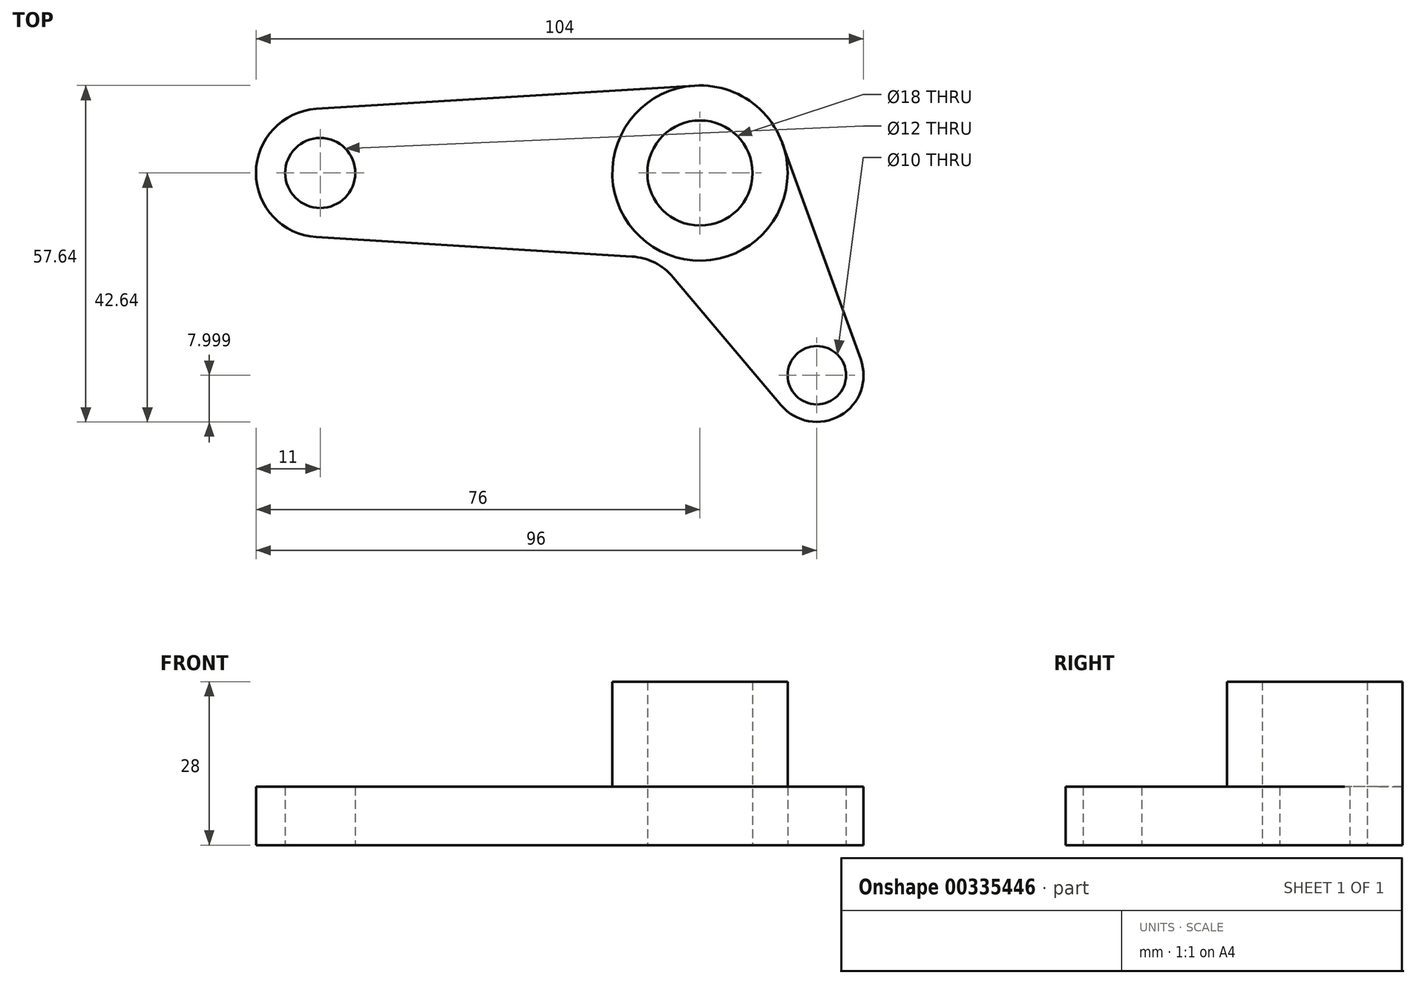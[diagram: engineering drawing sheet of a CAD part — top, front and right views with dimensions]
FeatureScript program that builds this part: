
annotation { "Feature Type Name" : "Feature", "Feature Type Description" : "" }
export const myFeature = defineFeature(function(context is Context, id is Id, definition is map)
    precondition{}
    {
        {
            var Q0;
            Q0=qCreatedBy(makeId("Top.planeOp"),FACE);
            var sketch = newSketch(context, id + "F0", { "sketchPlane" : qUnion([Q0])});
            skCircle(sketch, "E0", {"center": v(0, 0) * mm, "radius": 9 * mm});
            skCircle(sketch, "E1", {"center": v(0, 0) * mm, "radius": 15 * mm});
            skCircle(sketch, "E2", {"center": v(-65, 0) * mm, "radius": 6 * mm});
            skArc(sketch, "E3", {"start": v(-65.68, 10.98) * mm, "mid": v(-76, 0) * mm, "end": v(-65.68, -10.98) * mm});
            skCircle(sketch, "E4", {"center": v(20, -34.64) * mm, "radius": 5 * mm});
            skArc(sketch, "E5", {"start": v(13.88, -39.8) * mm, "mid": v(24, -41.57) * mm, "end": v(27.52, -31.92) * mm});
            skLineSegment(sketch, "E6", {"start": v(-65.68, 10.98) * mm, "end": v(-0.92, 14.97) * mm});
            skLineSegment(sketch, "E7", {"start": v(14.1, 5.11) * mm, "end": v(27.52, -31.92) * mm});
            skLineSegment(sketch, "E8", {"start": v(-65.68, -10.98) * mm, "end": v(-11.62, -14.31) * mm});
            skLineSegment(sketch, "E9", {"start": v(13.88, -39.8) * mm, "end": v(-4.58, -17.85) * mm});
            skArc(sketch, "E10", {"start": v(-4.58, -17.85) * mm, "mid": v(-7.73, -15.36) * mm, "end": v(-11.62, -14.31) * mm});
            skSolve(sketch);
        }
        {
            var Q0;
            Q0=makeQuery(id+"F0.imprint","IMPRINT",FACE,{"disambiguationData":[TD([[makeQuery(id+"F0.imprint","IMPRINT",EDGE,{"derivedFrom":sQuery(id+"F0.wireOp",EDGE,"E0")}),-1.0]])]});
            extrude(context, id + "F1", {"entities" : qUnion([Q0]), "depth" : 28 * mm});
        }
        {
            var Q0;
            Q0 = qSketchRegion(id + "F0", true);
            extrude(context, id + "F2", {"entities" : qUnion([Q0]), "operationType" : NewBodyOperationType.ADD, "depth" : 10 * mm});
        }
    });
